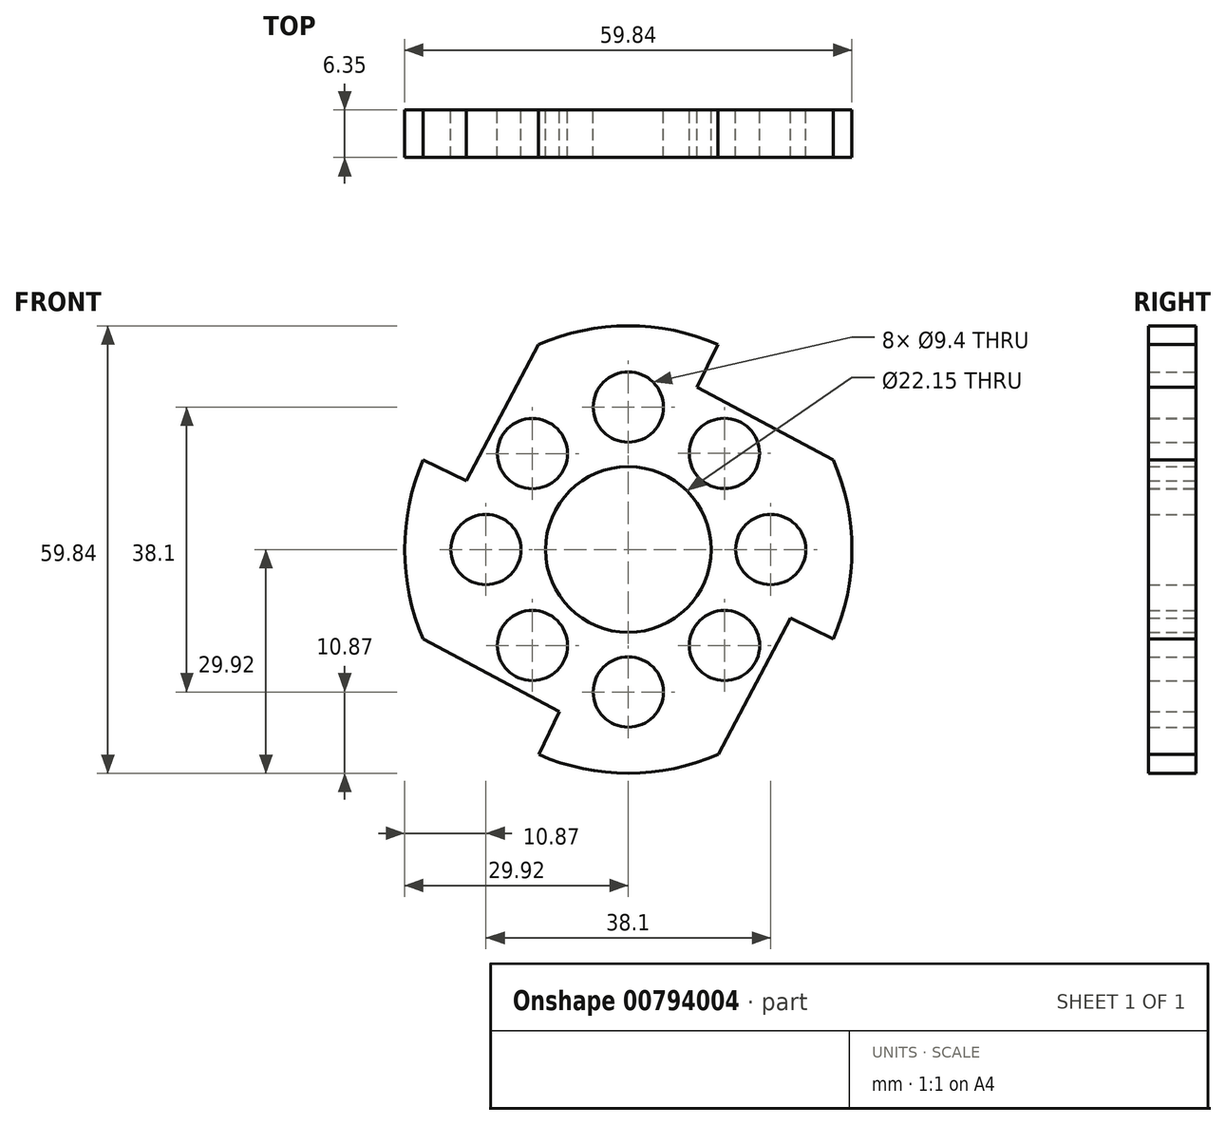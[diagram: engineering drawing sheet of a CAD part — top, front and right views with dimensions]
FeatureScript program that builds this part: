
annotation { "Feature Type Name" : "Feature", "Feature Type Description" : "" }
export const myFeature = defineFeature(function(context is Context, id is Id, definition is map)
    precondition{}
    {
        {
            var Q0;
            Q0=qCreatedBy(makeId("Front.planeOp"),FACE);
            var sketch = newSketch(context, id + "F0", { "sketchPlane" : qUnion([Q0])});
            skCircle(sketch, "E0", {"center": v(0, 0) * mm, "radius": 11.07 * mm});
            skArc(sketch, "E1", {"start": v(-27.41, 11.98) * mm, "mid": v(-29.92, 0) * mm, "end": v(-27.41, -11.98) * mm});
            skLineSegment(sketch, "E2", {"start": v(0, 0) * mm, "end": v(0, 19.05) * mm});
            skLineSegment(sketch, "E3", {"start": v(0, 0) * mm, "end": v(0, -19.05) * mm});
            skLineSegment(sketch, "E4", {"start": v(0, 0) * mm, "end": v(19.05, 0) * mm});
            skLineSegment(sketch, "E5", {"start": v(0, 0) * mm, "end": v(-19.05, 0) * mm});
            skCircle(sketch, "E6", {"center": v(0, -19.05) * mm, "radius": 4.7 * mm});
            skCircle(sketch, "E7", {"center": v(0, 19.05) * mm, "radius": 4.7 * mm});
            skCircle(sketch, "E8", {"center": v(19.05, 0) * mm, "radius": 4.7 * mm});
            skCircle(sketch, "E9", {"center": v(-19.05, 0) * mm, "radius": 4.7 * mm});
            skCircle(sketch, "E10", {"center": v(-12.83, -12.83) * mm, "radius": 4.7 * mm});
            skCircle(sketch, "E11", {"center": v(12.87, -12.83) * mm, "radius": 4.7 * mm});
            skCircle(sketch, "E12", {"center": v(12.85, 12.85) * mm, "radius": 4.7 * mm});
            skCircle(sketch, "E13", {"center": v(-12.83, 12.83) * mm, "radius": 4.7 * mm});
            skLineSegment(sketch, "E14", {"start": v(0, 19.05) * mm, "end": v(12.85, 12.85) * mm});
            skLineSegment(sketch, "E15", {"start": v(19.05, 0) * mm, "end": v(12.85, 12.85) * mm});
            skLineSegment(sketch, "E16", {"start": v(19.05, 0) * mm, "end": v(12.87, -12.83) * mm});
            skLineSegment(sketch, "E17", {"start": v(12.87, -12.83) * mm, "end": v(0, -19.05) * mm});
            skLineSegment(sketch, "E18", {"start": v(0, -19.05) * mm, "end": v(-12.83, -12.83) * mm});
            skLineSegment(sketch, "E19", {"start": v(-12.83, -12.83) * mm, "end": v(-19.05, 0) * mm});
            skLineSegment(sketch, "E20", {"start": v(-19.05, 0) * mm, "end": v(-12.83, 12.83) * mm});
            skLineSegment(sketch, "E21", {"start": v(-12.83, 12.83) * mm, "end": v(0, 19.05) * mm});
            skLineSegment(sketch, "E22", {"start": v(-15.94, -6.41) * mm, "end": v(-27.41, -11.98) * mm});
            skLineSegment(sketch, "E23", {"start": v(-6.41, -15.94) * mm, "end": v(-11.98, -27.41) * mm});
            skLineSegment(sketch, "E24", {"start": v(6.42, 15.95) * mm, "end": v(11.96, 27.42) * mm});
            skLineSegment(sketch, "E25", {"start": v(15.96, -6.41) * mm, "end": v(27.43, -11.94) * mm});
            skLineSegment(sketch, "E26", {"start": v(-15.94, 6.41) * mm, "end": v(-27.41, 11.98) * mm});
            skLineSegment(sketch, "E27", {"start": v(15.95, 6.42) * mm, "end": v(27.42, 11.96) * mm});
            skLineSegment(sketch, "E28", {"start": v(6.43, -15.94) * mm, "end": v(12.02, -27.4) * mm});
            skLineSegment(sketch, "E29", {"start": v(-6.41, 15.94) * mm, "end": v(-12, 27.4) * mm});
            skLineSegment(sketch, "E30", {"start": v(-21.68, 9.2) * mm, "end": v(-12, 27.4) * mm});
            skLineSegment(sketch, "E31", {"start": v(21.7, -9.18) * mm, "end": v(12.02, -27.4) * mm});
            skLineSegment(sketch, "E32", {"start": v(-9.2, -21.68) * mm, "end": v(-27.41, -11.98) * mm});
            skLineSegment(sketch, "E33", {"start": v(9.2, 21.68) * mm, "end": v(27.42, 11.96) * mm});
            skArc(sketch, "E34.trimOffspring", {"start": v(11.96, 27.42) * mm, "mid": v(-0.02, 29.92) * mm, "end": v(-12, 27.4) * mm});
            skArc(sketch, "E35.trimOffspring", {"start": v(27.43, -11.94) * mm, "mid": v(29.92, 0.01) * mm, "end": v(27.42, 11.96) * mm});
            skArc(sketch, "E36.trimOffspring", {"start": v(-11.98, -27.41) * mm, "mid": v(0.02, -29.92) * mm, "end": v(12.02, -27.4) * mm});
            skSolve(sketch);
        }
        {
            var Q0;
            {var subQ6=sQuery(id+"F0.wireOp",EDGE,"E29");Q0=makeQuery(id+"F0.imprint","IMPRINT",FACE,{"disambiguationData":[TD([[makeQuery(id+"F0.imprint","IMPRINT",EDGE,{"derivedFrom":subQ6}),-1.0]])]});}
            var Q1;
            {var subQ4=sQuery(id+"F0.wireOp",EDGE,"E29");Q1=makeQuery(id+"F0.imprint","IMPRINT",FACE,{"disambiguationData":[TD([[makeQuery(id+"F0.imprint","IMPRINT",EDGE,{"derivedFrom":subQ4}),1.0]])]});}
            var Q2;
            {var subQ8=sQuery(id+"F0.wireOp",EDGE,"E1");Q2=makeQuery(id+"F0.imprint","IMPRINT",FACE,{"disambiguationData":[TD([[makeQuery(id+"F0.imprint","IMPRINT",EDGE,{"derivedFrom":subQ8}),1.0]])]});}
            var Q3;
            {var subQ0=sQuery(id+"F0.wireOp",EDGE,"E22");Q3=makeQuery(id+"F0.imprint","IMPRINT",FACE,{"disambiguationData":[TD([[makeQuery(id+"F0.imprint","IMPRINT",EDGE,{"derivedFrom":subQ0}),1.0]])]});}
            var Q4;
            {var subQ4=sQuery(id+"F0.wireOp",EDGE,"E28");Q4=makeQuery(id+"F0.imprint","IMPRINT",FACE,{"disambiguationData":[TD([[makeQuery(id+"F0.imprint","IMPRINT",EDGE,{"derivedFrom":subQ4}),-1.0]])]});}
            var Q5;
            {var subQ4=sQuery(id+"F0.wireOp",EDGE,"E28");Q5=makeQuery(id+"F0.imprint","IMPRINT",FACE,{"disambiguationData":[TD([[makeQuery(id+"F0.imprint","IMPRINT",EDGE,{"derivedFrom":subQ4}),1.0]])]});}
            var Q6;
            {var subQ6=sQuery(id+"F0.wireOp",EDGE,"E27");Q6=makeQuery(id+"F0.imprint","IMPRINT",FACE,{"disambiguationData":[TD([[makeQuery(id+"F0.imprint","IMPRINT",EDGE,{"derivedFrom":subQ6}),-1.0]])]});}
            var Q7;
            {var subQ6=sQuery(id+"F0.wireOp",EDGE,"E27");Q7=makeQuery(id+"F0.imprint","IMPRINT",FACE,{"disambiguationData":[TD([[makeQuery(id+"F0.imprint","IMPRINT",EDGE,{"derivedFrom":subQ6}),1.0]])]});}
            var Q8;
            {var subQ1=sQuery(id+"F0.wireOp",EDGE,"E2");var subQ6=sQuery(id+"F0.wireOp",EDGE,"E0");var subQ12=makeQuery(id+"F0.imprint","INTERSECT",VERTEX,{"derivedFrom":[subQ6,subQ1]});Q8=makeQuery(id+"F0.imprint","IMPRINT",FACE,{"disambiguationData":[TD([[makeQuery(id+"F0.imprint","IMPRINT",EDGE,{"disambiguationData":[TD([[subQ12,-1.0]])],"derivedFrom":subQ6}),-1.0]])]});}
            var Q9;
            {var subQ5=sQuery(id+"F0.wireOp",EDGE,"E5");var subQ6=sQuery(id+"F0.wireOp",EDGE,"E0");var subQ7=makeQuery(id+"F0.imprint","INTERSECT",VERTEX,{"derivedFrom":[subQ6,subQ5]});Q9=makeQuery(id+"F0.imprint","IMPRINT",FACE,{"disambiguationData":[TD([[makeQuery(id+"F0.imprint","IMPRINT",EDGE,{"disambiguationData":[TD([[subQ7,-1.0]])],"derivedFrom":subQ6}),-1.0]])]});}
            var Q10;
            {var subQ8=sQuery(id+"F0.wireOp",EDGE,"E4");var subQ9=sQuery(id+"F0.wireOp",EDGE,"E0");var subQ10=makeQuery(id+"F0.imprint","INTERSECT",VERTEX,{"derivedFrom":[subQ9,subQ8]});Q10=makeQuery(id+"F0.imprint","IMPRINT",FACE,{"disambiguationData":[TD([[makeQuery(id+"F0.imprint","IMPRINT",EDGE,{"disambiguationData":[TD([[subQ10,1.0]])],"derivedFrom":subQ9}),-1.0]])]});}
            var Q11;
            {var subQ1=sQuery(id+"F0.wireOp",EDGE,"E0");var subQ8=sQuery(id+"F0.wireOp",EDGE,"E2");var subQ15=makeQuery(id+"F0.imprint","INTERSECT",VERTEX,{"derivedFrom":[subQ1,subQ8]});Q11=makeQuery(id+"F0.imprint","IMPRINT",FACE,{"disambiguationData":[TD([[makeQuery(id+"F0.imprint","IMPRINT",EDGE,{"disambiguationData":[TD([[subQ15,1.0]])],"derivedFrom":subQ1}),-1.0]])]});}
            extrude(context, id + "F1", {"entities" : qUnion([Q0, Q1, Q2, Q3, Q4, Q5, Q6, Q7, Q8, Q9, Q10, Q11]), "depth" : 6.35 * mm, "offsetDistance" : 25.4 * mm});
        }
    });
